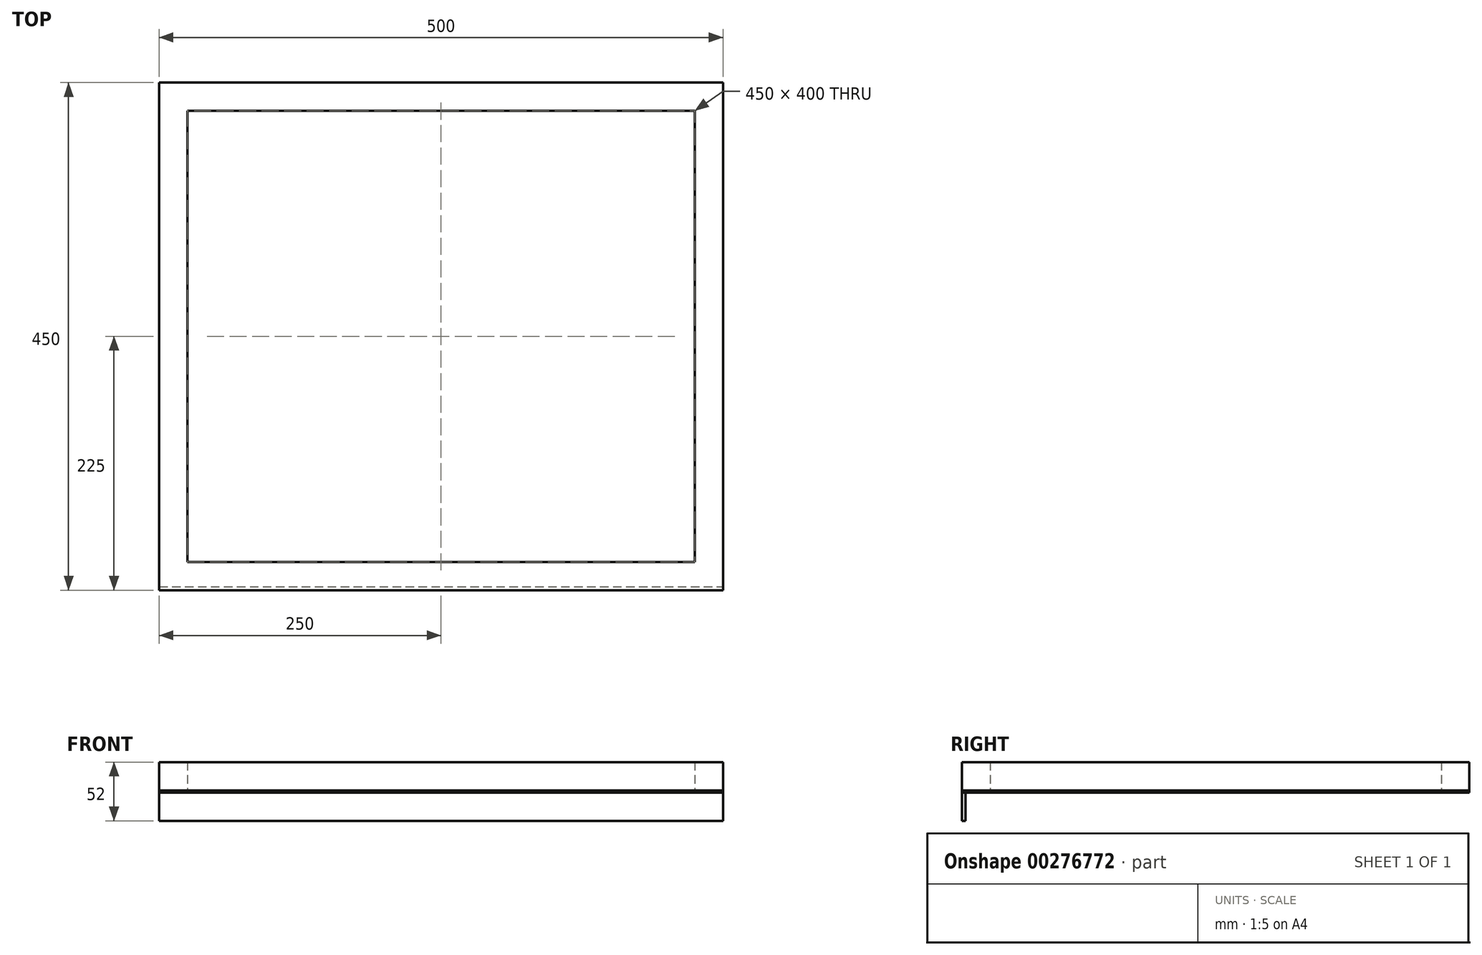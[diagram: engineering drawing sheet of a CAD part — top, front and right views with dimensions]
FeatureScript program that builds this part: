
annotation { "Feature Type Name" : "Feature", "Feature Type Description" : "" }
export const myFeature = defineFeature(function(context is Context, id is Id, definition is map)
    precondition{}
    {
        {
            var Q0;
            Q0=qCreatedBy(makeId("Top.planeOp"),FACE);
            var sketch = newSketch(context, id + "F0", { "sketchPlane" : qUnion([Q0])});
            skLineSegment(sketch, "E0.bottom", {"start": v(250, 225) * mm, "end": v(-250, 225) * mm});
            skLineSegment(sketch, "E0.top", {"start": v(250, -225) * mm, "end": v(-250, -225) * mm});
            skLineSegment(sketch, "E0.left", {"start": v(250, 225) * mm, "end": v(250, -225) * mm});
            skLineSegment(sketch, "E0.right", {"start": v(-250, 225) * mm, "end": v(-250, -225) * mm});
            skPoint(sketch, "E0.middle", {"position": v(0, 0) * mm});
            skLineSegment(sketch, "E1.0", {"start": v(225, 200) * mm, "end": v(-225, 200) * mm});
            skLineSegment(sketch, "E1.1", {"start": v(225, 200) * mm, "end": v(225, -200) * mm});
            skLineSegment(sketch, "E1.2", {"start": v(225, -200) * mm, "end": v(-225, -200) * mm});
            skLineSegment(sketch, "E1.3", {"start": v(-225, 200) * mm, "end": v(-225, -200) * mm});
            skSolve(sketch);
        }
        {
            var Q0;
            Q0=makeQuery(id+"F0.imprint","IMPRINT",FACE,{"disambiguationData":[TD([[makeQuery(id+"F0.imprint","IMPRINT",EDGE,{"derivedFrom":sQuery(id+"F0.wireOp",EDGE,"E0.bottom")}),1.0]])]});
            var Q1;
            Q1=makeQuery(id+"F0.imprint","IMPRINT",FACE,{"disambiguationData":[TD([[makeQuery(id+"F0.imprint","IMPRINT",EDGE,{"derivedFrom":sQuery(id+"F0.wireOp",EDGE,"E1.0")}),1.0]])]});
            extrude(context, id + "F1", {"entities" : qUnion([Q0, Q1]), "depth" : 2 * mm});
        }
        {
            var Q0;
            Q0=makeQuery(id+"F0.imprint","IMPRINT",FACE,{"disambiguationData":[TD([[makeQuery(id+"F0.imprint","IMPRINT",EDGE,{"derivedFrom":sQuery(id+"F0.wireOp",EDGE,"E0.bottom")}),1.0]])]});
            extrude(context, id + "F2", {"entities" : qUnion([Q0]), "depth" : 27 * mm});
        }
        {
            var Q0;
            Q0=makeQuery(id+"F2.opExtrude","SWEPT_FACE",FACE,{"disambiguationData":[OSD([sQuery(id+"F0.wireOp",EDGE,"E0.left")])]});
            var sketch = newSketch(context, id + "F3", { "sketchPlane" : qUnion([Q0])});
            skLineSegment(sketch, "E2", {"start": v(-225, 0) * mm, "end": v(-225, -25) * mm});
            skLineSegment(sketch, "E3", {"start": v(-225, -25) * mm, "end": v(-222, -25) * mm});
            skLineSegment(sketch, "E4", {"start": v(-222, -25) * mm, "end": v(-222, 0) * mm});
            skSolve(sketch);
        }
        {
            var Q0;
            {var subQ0=sQuery(id+"F3.wireOp",EDGE,"E2");Q0=makeQuery(id+"F3.imprint","IMPRINT",FACE,{"disambiguationData":[TD([[makeQuery(id+"F3.imprint","IMPRINT",EDGE,{"derivedFrom":subQ0}),1.0]])]});}
            extrude(context, id + "F4", {"entities" : qUnion([Q0]), "oppositeDirection" : true, "depth" : 500 * mm});
        }
    });
